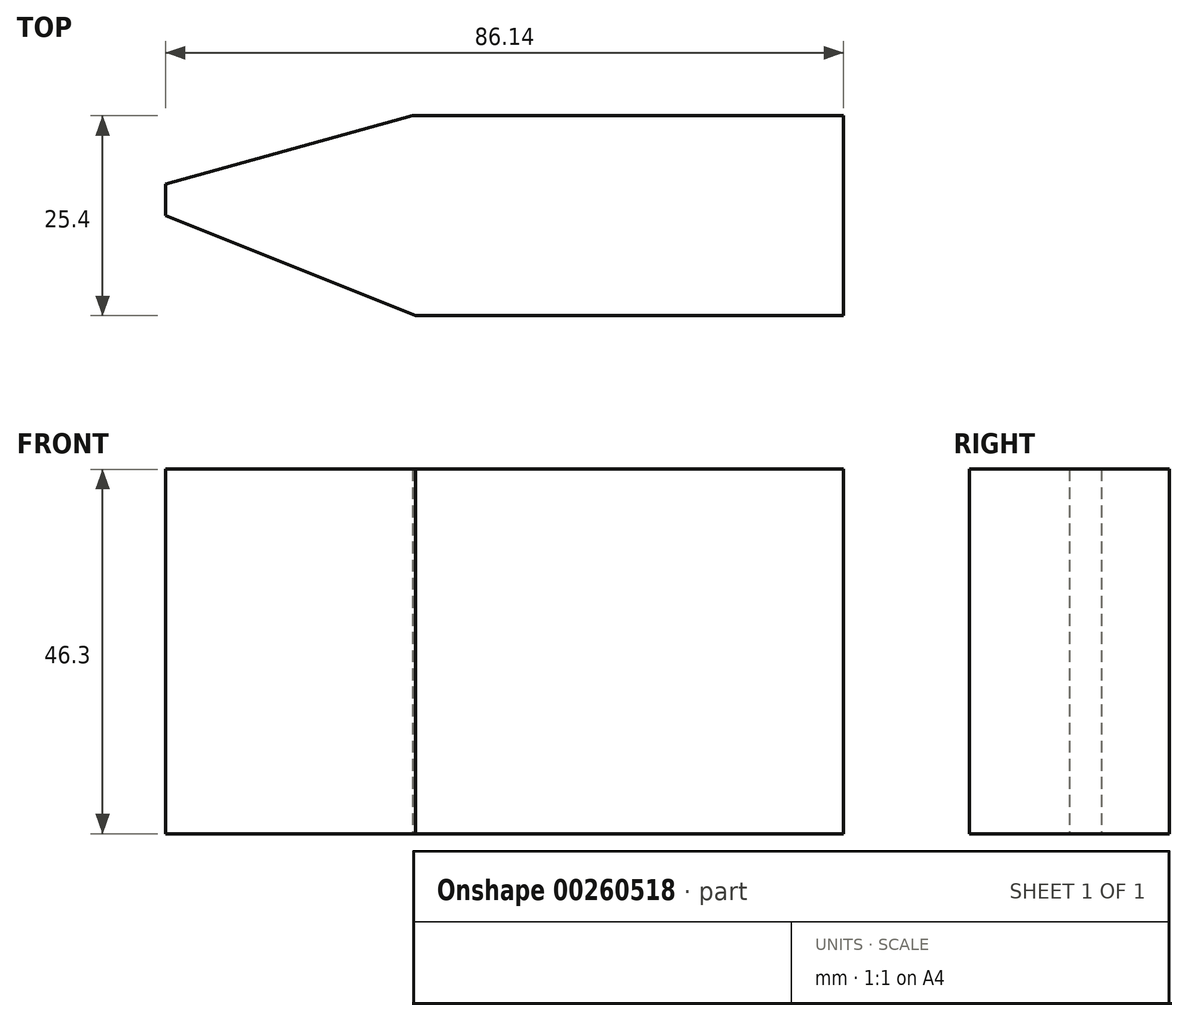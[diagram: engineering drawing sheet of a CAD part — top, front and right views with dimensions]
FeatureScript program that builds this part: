
annotation { "Feature Type Name" : "Feature", "Feature Type Description" : "" }
export const myFeature = defineFeature(function(context is Context, id is Id, definition is map)
    precondition{}
    {
        {
            var Q0;
            Q0=qCreatedBy(makeId("Front.planeOp"),FACE);
            var sketch = newSketch(context, id + "F0", { "sketchPlane" : qUnion([Q0])});
            skLineSegment(sketch, "E0.bottom", {"start": v(-41.97, 12) * mm, "end": v(44.17, 12) * mm});
            skLineSegment(sketch, "E0.top", {"start": v(-41.97, -34.31) * mm, "end": v(44.17, -34.31) * mm});
            skLineSegment(sketch, "E0.left", {"start": v(-41.97, 12) * mm, "end": v(-41.97, -34.31) * mm});
            skLineSegment(sketch, "E0.right", {"start": v(44.17, 12) * mm, "end": v(44.17, -34.31) * mm});
            skSolve(sketch);
        }
        {
            var Q0;
            Q0=makeQuery(id+"F0.imprint","IMPRINT",FACE,{"disambiguationData":[TD([[makeQuery(id+"F0.imprint","IMPRINT",EDGE,{"derivedFrom":sQuery(id+"F0.wireOp",EDGE,"E0.bottom")}),-1.0]])]});
            extrude(context, id + "F1", {"entities" : qUnion([Q0]), "depth" : 25.4 * mm});
        }
        {
            var Q0;
            Q0=makeQuery(id+"F1.opExtrude","SWEPT_FACE",FACE,{"disambiguationData":[OSD([sQuery(id+"F0.wireOp",EDGE,"E0.top")])]});
            var sketch = newSketch(context, id + "F2", { "sketchPlane" : qUnion([Q0])});
            skLineSegment(sketch, "E1", {"start": v(-10.24, 25.4) * mm, "end": v(-41.97, 12.7) * mm});
            skLineSegment(sketch, "E2", {"start": v(-10.57, 0) * mm, "end": v(-41.97, 9.32) * mm});
            skSolve(sketch);
        }
        {
            var Q0;
            {var subQ0=sQuery(id+"F2.wireOp",EDGE,"E1");Q0=makeQuery(id+"F2.imprint","IMPRINT",FACE,{"disambiguationData":[TD([[makeQuery(id+"F2.imprint","IMPRINT",EDGE,{"derivedFrom":subQ0}),-1.0]])]});}
            extrude(context, id + "F3", {"entities" : qUnion([Q0]), "operationType" : NewBodyOperationType.REMOVE, "oppositeDirection" : true, "depth" : 48.26 * mm});
        }
        {
            var Q0;
            Q0=makeQuery(id+"F1.opExtrude","SWEPT_FACE",FACE,{"disambiguationData":[OSD([sQuery(id+"F0.wireOp",EDGE,"E0.top")])]});
            var sketch = newSketch(context, id + "F4", { "sketchPlane" : qUnion([Q0])});
            skLineSegment(sketch, "E3", {"start": v(-10.57, 0) * mm, "end": v(-41.97, 8.65) * mm});
            skSolve(sketch);
        }
        {
            var Q0;
            {var subQ0=sQuery(id+"F4.wireOp",EDGE,"E3");Q0=makeQuery(id+"F4.imprint","IMPRINT",FACE,{"disambiguationData":[TD([[makeQuery(id+"F4.imprint","IMPRINT",EDGE,{"derivedFrom":subQ0}),1.0]])]});}
            extrude(context, id + "F5", {"entities" : qUnion([Q0]), "operationType" : NewBodyOperationType.REMOVE, "oppositeDirection" : true, "depth" : 50.8 * mm});
        }
    });
